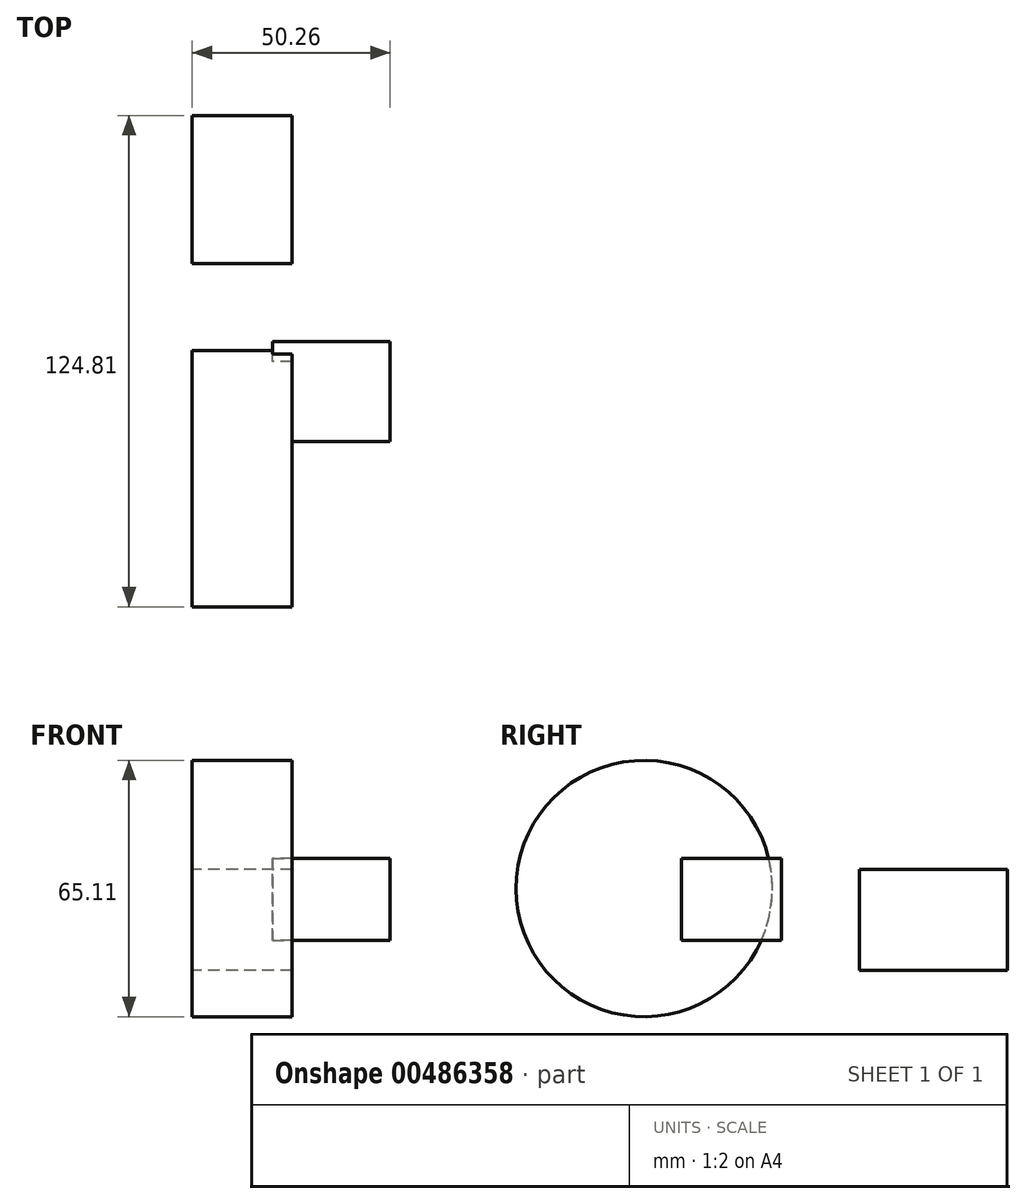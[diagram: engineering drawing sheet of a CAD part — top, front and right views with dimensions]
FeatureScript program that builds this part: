
annotation { "Feature Type Name" : "Feature", "Feature Type Description" : "" }
export const myFeature = defineFeature(function(context is Context, id is Id, definition is map)
    precondition{}
    {
        {
            var Q0;
            Q0=qCreatedBy(makeId("Front.planeOp"),FACE);
            var sketch = newSketch(context, id + "F0", { "sketchPlane" : qUnion([Q0])});
            skLineSegment(sketch, "E0", {"start": v(-39.44, 50.68) * mm, "end": v(-39.44, 29.61) * mm});
            skLineSegment(sketch, "E1", {"start": v(-39.44, 29.61) * mm, "end": v(-14.38, 29.61) * mm});
            skLineSegment(sketch, "E2", {"start": v(-14.38, 29.61) * mm, "end": v(-14.38, 49.26) * mm});
            skLineSegment(sketch, "E3", {"start": v(-14.38, 49.26) * mm, "end": v(-39.44, 49.26) * mm});
            skLineSegment(sketch, "E4.bottom", {"start": v(20.36, 49.54) * mm, "end": v(50.26, 49.54) * mm});
            skLineSegment(sketch, "E4.top", {"start": v(20.36, 28.76) * mm, "end": v(50.26, 28.76) * mm});
            skLineSegment(sketch, "E4.left", {"start": v(20.36, 49.54) * mm, "end": v(20.36, 28.76) * mm});
            skLineSegment(sketch, "E4.right", {"start": v(50.26, 49.54) * mm, "end": v(50.26, 28.76) * mm});
            skLineSegment(sketch, "E5.bottom", {"start": v(-49.12, -20.79) * mm, "end": v(-16.94, -20.79) * mm});
            skLineSegment(sketch, "E5.top", {"start": v(-49.12, -47.84) * mm, "end": v(-16.94, -47.84) * mm});
            skLineSegment(sketch, "E5.left", {"start": v(-49.12, -20.79) * mm, "end": v(-49.12, -47.84) * mm});
            skLineSegment(sketch, "E5.right", {"start": v(-16.94, -20.79) * mm, "end": v(-16.94, -47.84) * mm});
            skLineSegment(sketch, "E6.bottom", {"start": v(24.07, -18.22) * mm, "end": v(59.66, -18.22) * mm});
            skLineSegment(sketch, "E6.top", {"start": v(24.07, -47.84) * mm, "end": v(59.66, -47.84) * mm});
            skLineSegment(sketch, "E6.left", {"start": v(24.07, -18.22) * mm, "end": v(24.07, -47.84) * mm});
            skLineSegment(sketch, "E6.right", {"start": v(59.66, -18.22) * mm, "end": v(59.66, -47.84) * mm});
            skSolve(sketch);
        }
        {
            var Q0;
            Q0=makeQuery(id+"F0.imprint","IMPRINT",FACE,{"disambiguationData":[TD([[makeQuery(id+"F0.imprint","IMPRINT",EDGE,{"derivedFrom":sQuery(id+"F0.wireOp",EDGE,"E4.bottom")}),-1.0]])]});
            extrude(context, id + "F1", {"entities" : qUnion([Q0]), "depth" : 25.4 * mm});
        }
        {
            var Q0;
            Q0=qCreatedBy(makeId("Right.planeOp"),FACE);
            var sketch = newSketch(context, id + "F2", { "sketchPlane" : qUnion([Q0])});
            skLineSegment(sketch, "E7.bottom", {"start": v(57.37, 46.7) * mm, "end": v(19.79, 46.7) * mm});
            skLineSegment(sketch, "E7.top", {"start": v(57.37, 21.07) * mm, "end": v(19.79, 21.07) * mm});
            skLineSegment(sketch, "E7.left", {"start": v(57.37, 46.7) * mm, "end": v(57.37, 21.07) * mm});
            skLineSegment(sketch, "E7.right", {"start": v(19.79, 46.7) * mm, "end": v(19.79, 21.07) * mm});
            skSolve(sketch);
        }
        {
            var Q0;
            Q0 = qSketchRegion(id + "F2", true);
            extrude(context, id + "F3", {"entities" : qUnion([Q0]), "depth" : 25.4 * mm});
        }
        {
            var Q0;
            Q0=qCreatedBy(makeId("Right.planeOp"),FACE);
            var sketch = newSketch(context, id + "F4", { "sketchPlane" : qUnion([Q0])});
            skCircle(sketch, "E8", {"center": v(-34.88, 41.88) * mm, "radius": 32.56 * mm});
            skSolve(sketch);
        }
        {
            var Q0;
            Q0=makeQuery(id+"F4.imprint","IMPRINT",FACE,{"disambiguationData":[TD([[makeQuery(id+"F4.imprint","IMPRINT",EDGE,{"derivedFrom":sQuery(id+"F4.wireOp",EDGE,"E8")}),1.0]])]});
            extrude(context, id + "F5", {"entities" : qUnion([Q0]), "operationType" : NewBodyOperationType.ADD, "depth" : 25.4 * mm});
        }
    });
